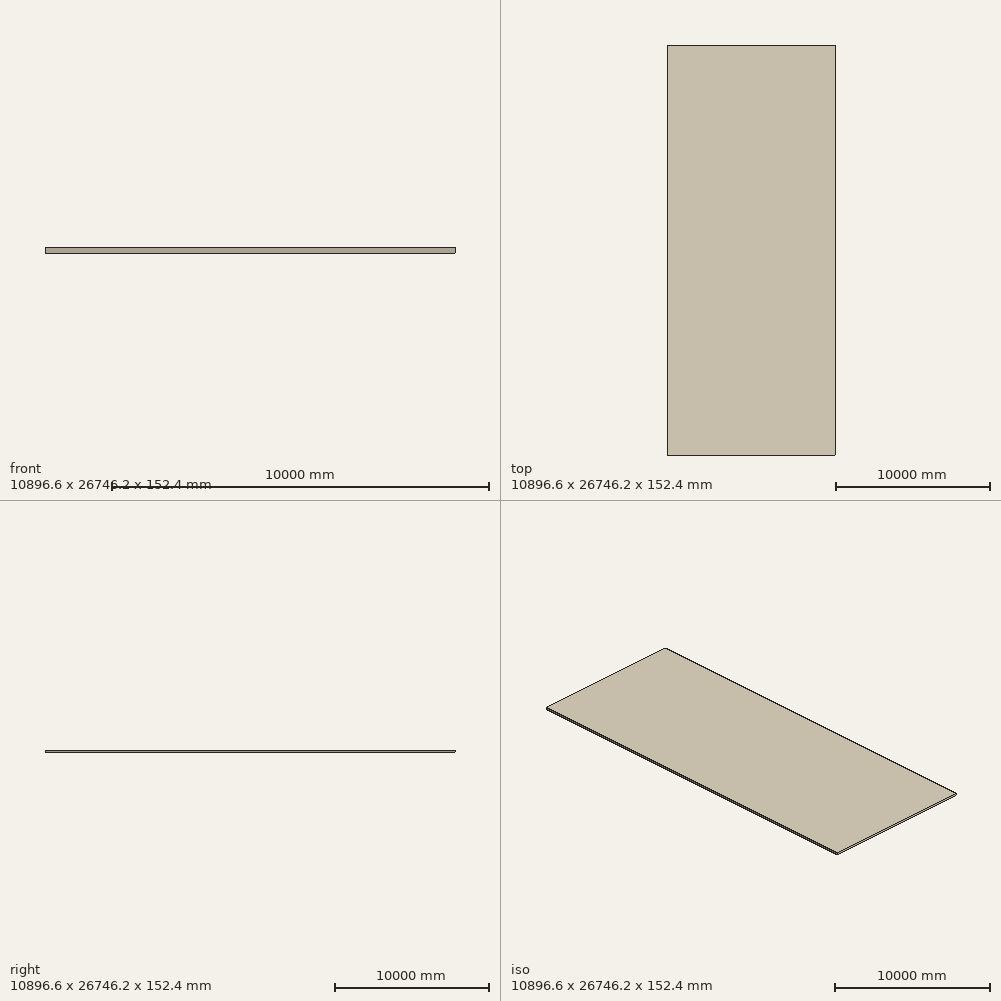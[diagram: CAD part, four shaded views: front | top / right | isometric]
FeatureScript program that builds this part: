
annotation { "Feature Type Name" : "Feature", "Feature Type Description" : "" }
export const myFeature = defineFeature(function(context is Context, id is Id, definition is map)
    precondition{}
    {
        {
            var Q0;
            Q0=qCreatedBy(makeId("Top.planeOp"),FACE);
            var sketch = newSketch(context, id + "F0", { "sketchPlane" : qUnion([Q0])});
            skLineSegment(sketch, "E0.bottom", {"start": v(-5448.3, -13373.1) * mm, "end": v(5448.3, -13373.1) * mm});
            skLineSegment(sketch, "E0.top", {"start": v(-5448.3, 13373.1) * mm, "end": v(5448.3, 13373.1) * mm});
            skLineSegment(sketch, "E0.left", {"start": v(-5448.3, -13373.1) * mm, "end": v(-5448.3, 13373.1) * mm});
            skLineSegment(sketch, "E0.right", {"start": v(5448.3, -13373.1) * mm, "end": v(5448.3, 13373.1) * mm});
            skPoint(sketch, "E0.middle", {"position": v(0, 0) * mm});
            skSolve(sketch);
        }
        {
            var Q0;
            Q0=makeQuery(id+"F0.imprint","IMPRINT",FACE,{"disambiguationData":[TD([[makeQuery(id+"F0.imprint","IMPRINT",EDGE,{"derivedFrom":sQuery(id+"F0.wireOp",EDGE,"E0.bottom")}),1.0]])]});
            extrude(context, id + "F1", {"entities" : qUnion([Q0]), "offsetDistance" : 30.48 * mm, "depth" : 152.4 * mm});
        }
    });
